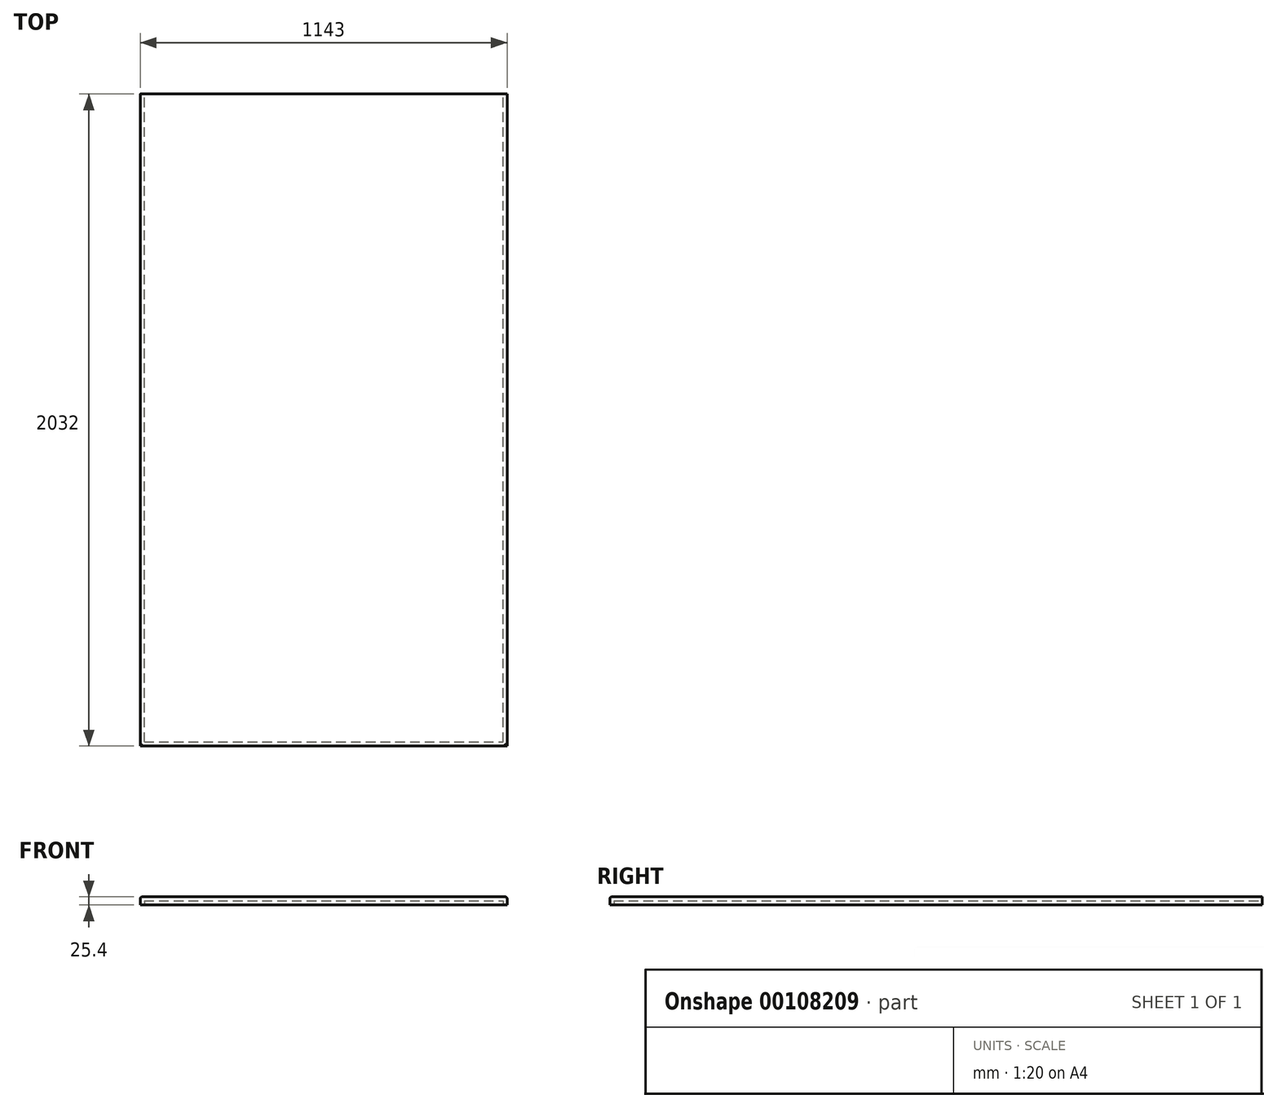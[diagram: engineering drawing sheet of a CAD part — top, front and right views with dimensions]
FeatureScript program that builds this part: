
annotation { "Feature Type Name" : "Feature", "Feature Type Description" : "" }
export const myFeature = defineFeature(function(context is Context, id is Id, definition is map)
    precondition{}
    {
        {
            var Q0;
            Q0=qCreatedBy(makeId("Top.planeOp"),FACE);
            var sketch = newSketch(context, id + "F0", { "sketchPlane" : qUnion([Q0])});
            skLineSegment(sketch, "E0.bottom", {"start": v(0, 0) * mm, "end": v(1143, 0) * mm});
            skLineSegment(sketch, "E0.top", {"start": v(0, 2032) * mm, "end": v(1143, 2032) * mm});
            skLineSegment(sketch, "E0.left", {"start": v(0, 0) * mm, "end": v(0, 2032) * mm});
            skLineSegment(sketch, "E0.right", {"start": v(1143, 0) * mm, "end": v(1143, 2032) * mm});
            skSolve(sketch);
        }
        {
            var Q0;
            Q0 = qSketchRegion(id + "F0", true);
            extrude(context, id + "F1", {"entities" : qUnion([Q0]), "depth" : 25.4 * mm});
        }
        {
            var Q0;
            Q0=makeQuery(id+"F1.opExtrude","CAP_FACE",FACE,{"disambiguationData":[OSD([sQuery(id+"F0.wireOp",EDGE,"E0.bottom"),sQuery(id+"F0.wireOp",EDGE,"E0.top"),sQuery(id+"F0.wireOp",EDGE,"E0.left"),sQuery(id+"F0.wireOp",EDGE,"E0.right")])],"isStart":true});
            var Q1;
            Q1=makeQuery(id+"F1.opExtrude","SWEPT_FACE",FACE,{"disambiguationData":[OSD([sQuery(id+"F0.wireOp",EDGE,"E0.top")])]});
            shell(context, id + "F2", {"entities" : qUnion([Q0, Q1]), "thickness" : 12.7 * mm});
        }
        {
            var Q0;
            Q0=makeQuery(id+"F1.opExtrude","CAP_EDGE",EDGE,{"disambiguationData":[OSD([sQuery(id+"F0.wireOp",EDGE,"E0.right")])],"isStart":false});
            var Q1;
            Q1=makeQuery(id+"F1.opExtrude","CAP_EDGE",EDGE,{"disambiguationData":[OSD([sQuery(id+"F0.wireOp",EDGE,"E0.bottom")])],"isStart":false});
            var Q2;
            Q2=makeQuery(id+"F1.opExtrude","CAP_EDGE",EDGE,{"disambiguationData":[OSD([sQuery(id+"F0.wireOp",EDGE,"E0.left")])],"isStart":false});
            fillet(context, id + "F3", {"entities" : qUnion([Q0, Q1, Q2]), "radius" : 6.35 * mm, "tangentPropagation" : true, "allowEdgeOverflow" : false});
        }
    });
